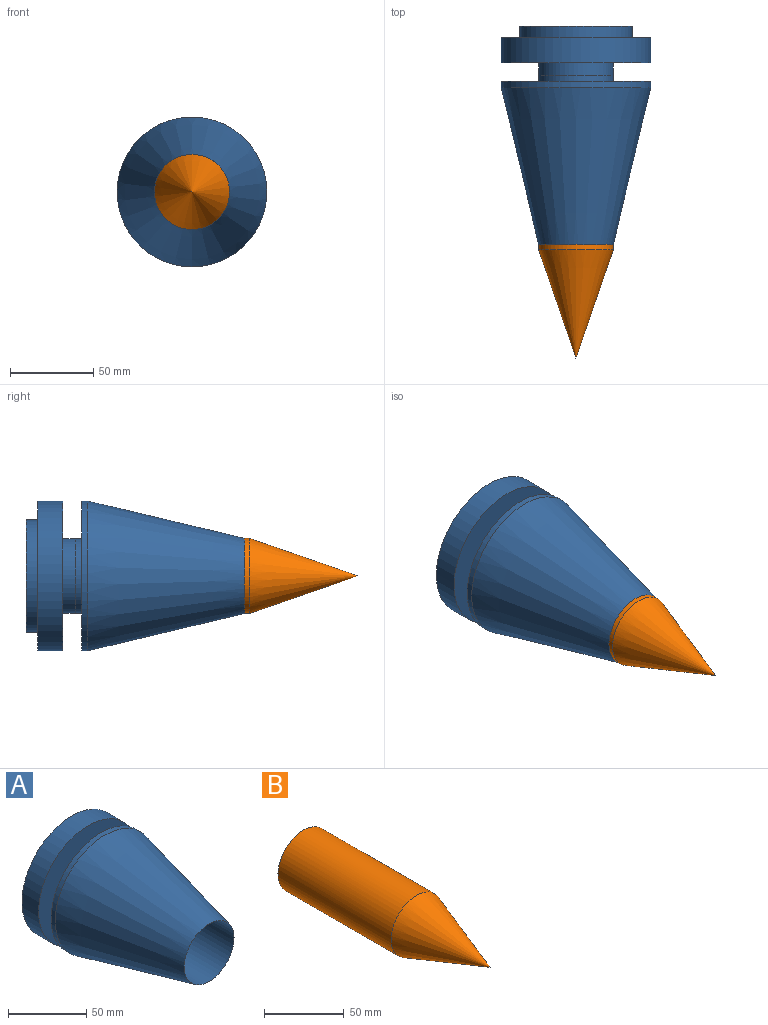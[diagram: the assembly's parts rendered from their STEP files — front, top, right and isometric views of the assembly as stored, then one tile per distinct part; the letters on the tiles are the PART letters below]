
ASSEMBLY  parts=2 mates=1
PART A: 12 faces, bbox 89.8x131x89.8 mm
  f0: cone r=22.5mm half-angle=13.4deg, axis (0,1,0), area 20458.7mm2, adj f1,f11
  f1: cylinder r=22.5mm len=94mm, axis (0,-1,0), area 13288.9mm2, adj f0,f2
  f2: plane 45x45mm, normal (0,-1,0), area 1590.4mm2, adj f1
  f3: plane 67.34x67.34mm, normal (0,1,0), area 3561.5mm2, adj f4
  f4: cylinder r=33.67mm len=67.34mm, axis (0,-1,0), area 1480.9mm2, adj f3,f5
  f5: plane 89.79x89.79mm, normal (0,1,0), area 2770mm2, adj f4,f6
  f6: cylinder r=44.89mm len=89.79mm, axis (0,-1,0), area 4231.1mm2, adj f5,f7
  f7: plane 89.79x89.79mm, normal (0,-1,0), area 4756.2mm2, adj f6,f8
  f8: cylinder r=22.39mm len=44.79mm, axis (0,-1,0), area 1055.2mm2, adj f7,f9
  f9: cone r=22.39mm half-angle=0.8deg, axis (0,-1,0), area 528.3mm2, adj f8,f10
  f10: plane 89.79x89.79mm, normal (0,1,0), area 4748.6mm2, adj f9,f11
  f11: cylinder r=44.89mm len=89.79mm, axis (0,-1,0), area 1057.8mm2, adj f0,f10
PART B: 3 faces, bbox 45x165x45 mm
  f0: plane 45x45mm, normal (0,1,0), area 1590.4mm2, adj f1
  f1: cylinder r=22.5mm len=100mm, axis (0,-1,0), area 14137.2mm2, adj f0,f2
  f2: cone r=22.5mm half-angle=19.1deg, axis (0,1,0), area 4862.1mm2, adj f1
PLACE A t=(-2.58,-192.37,173.6)mm
PLACE B rot(axis=(-0.12,-0.85,-0.51),0deg) t=(-2.58,-189.37,173.6)mm
MATE fastened A.f0 <-> B.f1  axis (0,-1,0) through (-2.58,-189.37,173.6)mm
